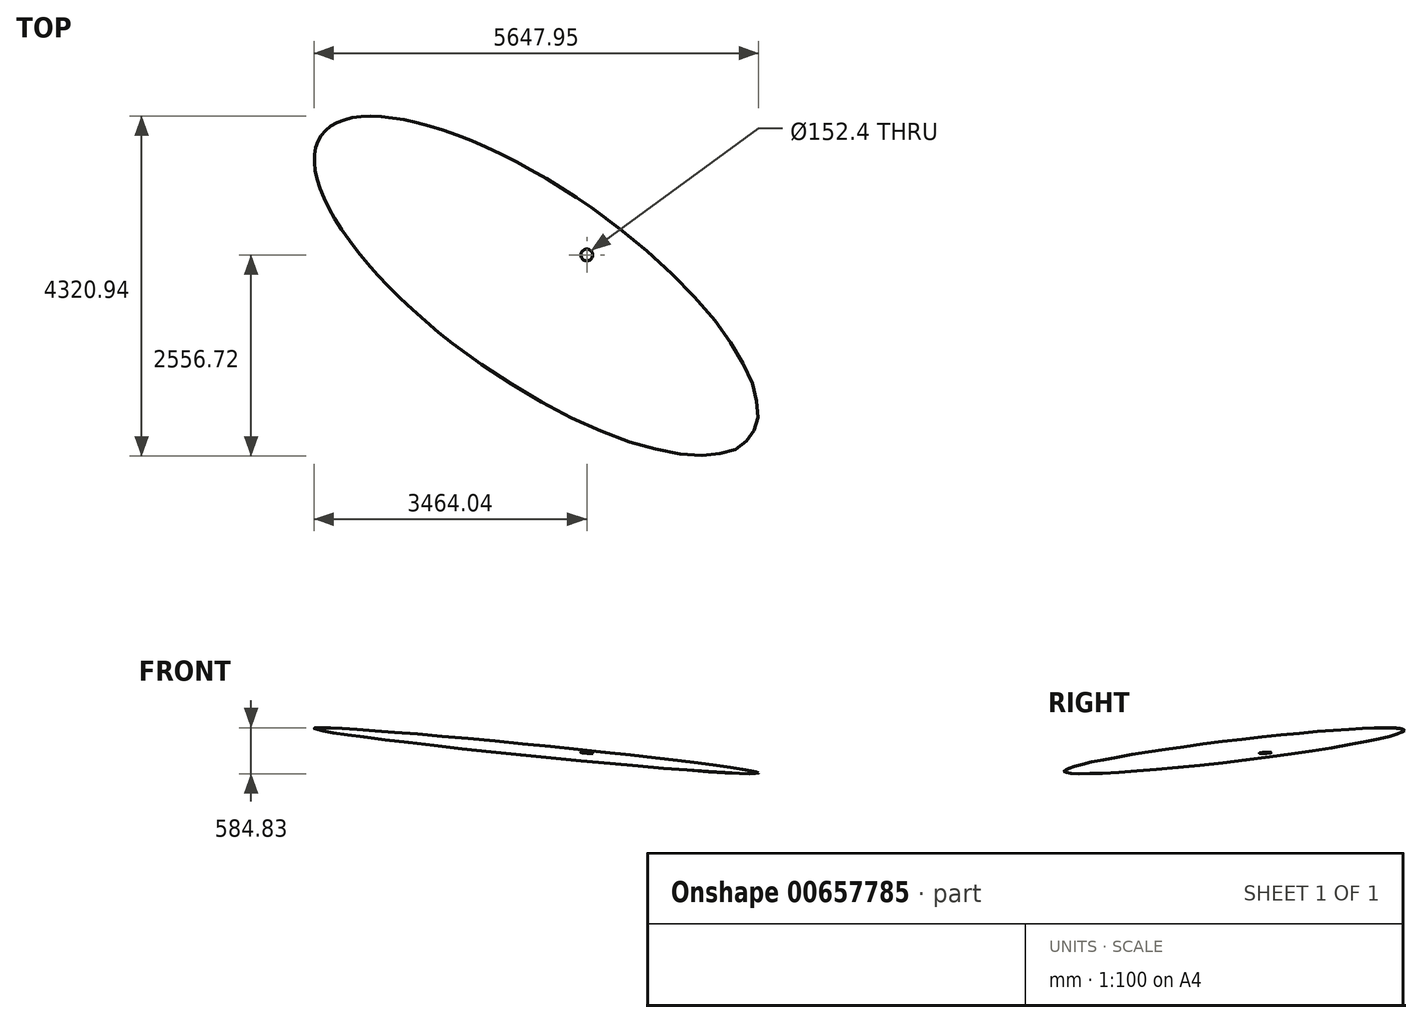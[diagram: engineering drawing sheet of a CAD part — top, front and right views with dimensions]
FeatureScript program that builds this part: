
annotation { "Feature Type Name" : "Feature", "Feature Type Description" : "" }
export const myFeature = defineFeature(function(context is Context, id is Id, definition is map)
    precondition{}
    {
        {
            assignVariable(context, id + "F0", {"name" : "Azimuth", "anyValue" : 35});
        }
        {
            assignVariable(context, id + "F1", {"name" : "Dip", "anyValue" : 5});
        }
        {
            assignVariable(context, id + "F2", {"name" : "Width", "anyValue" : .40});
        }
        {
            var Q0;
            Q0=qCreatedBy(makeId("Top.planeOp"),FACE);
            var sketch = newSketch(context, id + "F3", { "sketchPlane" : qUnion([Q0])});
            skEllipse(sketch, "E0", {"center": v(0, 0) * mm, "majorRadius": 1219.2 * mm, "minorRadius": 3352.8 * mm, "majorAxis": v(0, 1)});
            skLineSegment(sketch, "E1", {"start": v(0, 3810) * mm, "end": v(0, -3810) * mm, "construction": true});
            skLineSegment(sketch, "E2", {"start": v(-2286, 0) * mm, "end": v(2286, 0) * mm, "construction": true});
            skLineSegment(sketch, "E3.0", {"start": v(-640.08, 1219.2) * mm, "end": v(-640.08, -1219.2) * mm, "construction": true});
            skLineSegment(sketch, "E4.0", {"start": v(-3352.8, 396.24) * mm, "end": v(3352.8, 396.24) * mm, "construction": true});
            skSolve(sketch);
        }
        {
            var Q0;
            Q0=qCreatedBy(makeId("Top.planeOp"),FACE);
            var sketch = newSketch(context, id + "F4", { "sketchPlane" : qUnion([Q0])});
            skLineSegment(sketch, "E5", {"start": v(-640.08, 0) * mm, "end": v(0, 0) * mm});
            skLineSegment(sketch, "E6", {"start": v(-640.08, 396.24) * mm, "end": v(-640.08, 0) * mm});
            skSolve(sketch);
        }
        {
            var Q0;
            Q0=qSketchRegion(id+"F3",true);
            extrude(context, id + "F5", {"entities" : qUnion([Q0]), "depth" : (getVariable(context, 'Width')) * mm});
        }
        {
            var Q0;
            Q0=qCreatedBy(makeId("Front.planeOp"),FACE);
            var sketch = newSketch(context, id + "F6", { "sketchPlane" : qUnion([Q0])});
            skLineSegment(sketch, "E7", {"start": v(0, 0) * mm, "end": v(0, -5547.36) * mm, "construction": true});
            skSolve(sketch);
        }
        {
            var Q0;
            Q0=makeQuery(id+"F5.opExtrude","SWEPT_BODY",BODY,{"disambiguationData":[OSD([sQuery(id+"F3.wireOp",EDGE,"E0"),sQuery(id+"F3.wireOp",EDGE,"TMMzbr5i-4nV4-ZnMr-aG6B-IGJ66UyS6uPJ")])]});
            var Q1;
            Q1=sQuery(id+"F3.wireOp",EDGE,"E1");
            transform(context, id + "F7", {"entities" : qUnion([Q0]), "transformType" : TransformType.ROTATION, "transformAxis" : qUnion([Q1]), "angle" : (getVariable(context, 'Dip')) * degree, "oppositeDirection" : true, "makeCopy" : false});
        }
        {
            var Q0;
            Q0=makeQuery(id+"F5.opExtrude","SWEPT_BODY",BODY,{"disambiguationData":[OSD([sQuery(id+"F3.wireOp",EDGE,"E0")])]});
            var Q1;
            Q1=sQuery(id+"F6.wireOp",EDGE,"E7");
            transform(context, id + "F8", {"entities" : qUnion([Q0]), "transformType" : TransformType.ROTATION, "transformAxis" : qUnion([Q1]), "angle" : (getVariable(context, 'Azimuth')) * degree, "makeCopy" : false});
        }
        {
            var Q0;
            Q0=makeQuery(id+"F5.opExtrude","SWEPT_BODY",BODY,{"disambiguationData":[OSD([sQuery(id+"F3.wireOp",EDGE,"E0"),sQuery(id+"F3.wireOp",EDGE,"TMMzbr5i-4nV4-ZnMr-aG6B-IGJ66UyS6uPJ")])]});
            var Q1;
            Q1=sQuery(id+"F4.wireOp",EDGE,"E5");
            transform(context, id + "F9", {"entities" : qUnion([Q0]), "transformType" : TransformType.TRANSLATION_ENTITY, "oppositeDirectionEntity" : true, "transformLine" : qUnion([Q1]), "makeCopy" : false});
        }
        {
            var Q0;
            Q0=makeQuery(id+"F5.opExtrude","SWEPT_BODY",BODY,{"disambiguationData":[OSD([sQuery(id+"F3.wireOp",EDGE,"E0"),sQuery(id+"F3.wireOp",EDGE,"TMMzbr5i-4nV4-ZnMr-aG6B-IGJ66UyS6uPJ")])]});
            var Q1;
            Q1=sQuery(id+"F4.wireOp",EDGE,"E6");
            transform(context, id + "F10", {"entities" : qUnion([Q0]), "transformType" : TransformType.TRANSLATION_ENTITY, "oppositeDirectionEntity" : false, "transformLine" : qUnion([Q1]), "makeCopy" : false});
        }
        {
            var Q0;
            Q0=qCreatedBy(makeId("Top.planeOp"),FACE);
            var sketch = newSketch(context, id + "F11", { "sketchPlane" : qUnion([Q0])});
            skCircle(sketch, "E8", {"center": v(0, 0) * mm, "radius": 76.2 * mm});
            skSolve(sketch);
        }
        {
            var Q0;
            Q0=qSketchRegion(id+"F11",true);
            extrude(context, id + "F12", {"entities" : qUnion([Q0]), "operationType" : NewBodyOperationType.REMOVE, "endBound" : BoundingType.THROUGH_ALL, "oppositeDirection" : true, "depth" : 30.48 * mm, "hasSecondDirection" : true, "secondDirectionBound" : SecondDirectionBoundingType.THROUGH_ALL, "secondDirectionOppositeDirection" : false, "secondDirectionDepth" : 30.48 * mm});
        }
        {
            var Q0;
            Q0=qCreatedBy(makeId("Front.planeOp"),FACE);
            var sketch = newSketch(context, id + "F13", { "sketchPlane" : qUnion([Q0])});
            skLineSegment(sketch, "E9", {"start": v(0, -5547.36) * mm, "end": v(0, -13.75) * mm});
            skSolve(sketch);
        }
        {
            var Q0;
            Q0=makeQuery(id+"F5.opExtrude","SWEPT_BODY",BODY,{"disambiguationData":[OSD([sQuery(id+"F3.wireOp",EDGE,"E0")])]});
            var Q1;
            Q1=sQuery(id+"F13.wireOp",EDGE,"E9");
            transform(context, id + "F14", {"entities" : qUnion([Q0]), "transformType" : TransformType.TRANSLATION_ENTITY, "oppositeDirectionEntity" : true, "transformLine" : qUnion([Q1]), "makeCopy" : false});
        }
    });
